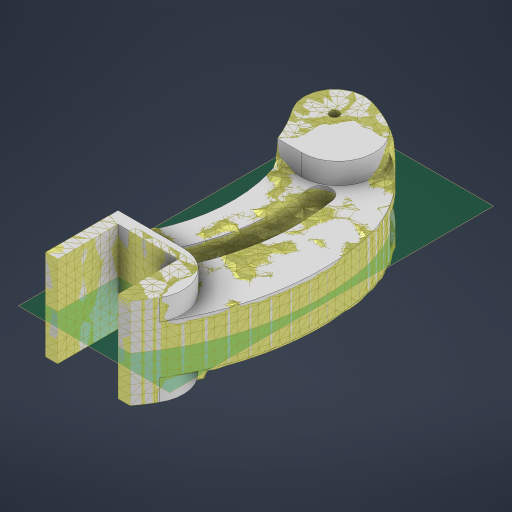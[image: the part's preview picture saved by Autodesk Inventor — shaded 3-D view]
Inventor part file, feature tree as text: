
AUTODESK INVENTOR PART (.ipt)
format: ipt  version: 2024 (Build 280153000, 153)  size: 515,584 bytes
history: native  units: mm
features: other x5, extrude x5, sketch x5, fillet x2, mirror x1
ambient origin geometry x8: Origin, YZ Plane, XZ Plane, XY Plane, X Axis, Y Axis, Z Axis, Center Point
bodies: Body1 (feature_tree)
feature tree (18):
  other  "Твердое тело1"
  extrude  "Выдавливание1"  Depth=20.0mm
  extrude  "Выдавливание2"  Depth=4.0mm
  other  "РабПлоскость1"
  extrude  "Выдавливание3"  Depth=4.0mm
  other  "shok_absorber_holder"
  extrude  "Выдавливание4"  Depth=30.0mm TaperAngle=0.0deg
  other  "РабПлоскость2"
  mirror  "Зеркальное отражение1"
  fillet  "Сопряжение1"  Radius=10.0mm
  fillet  "Сопряжение2"  Radius=3.0mm
  extrude  "Выдавливание5"  Depth=50.0mm
  sketch  "Эскиз1"
  sketch  "Эскиз2"
  sketch  "Эскиз4"
  sketch  "Эскиз5"
  sketch  "Эскиз6"
  other  "ЭлементСетки1"
